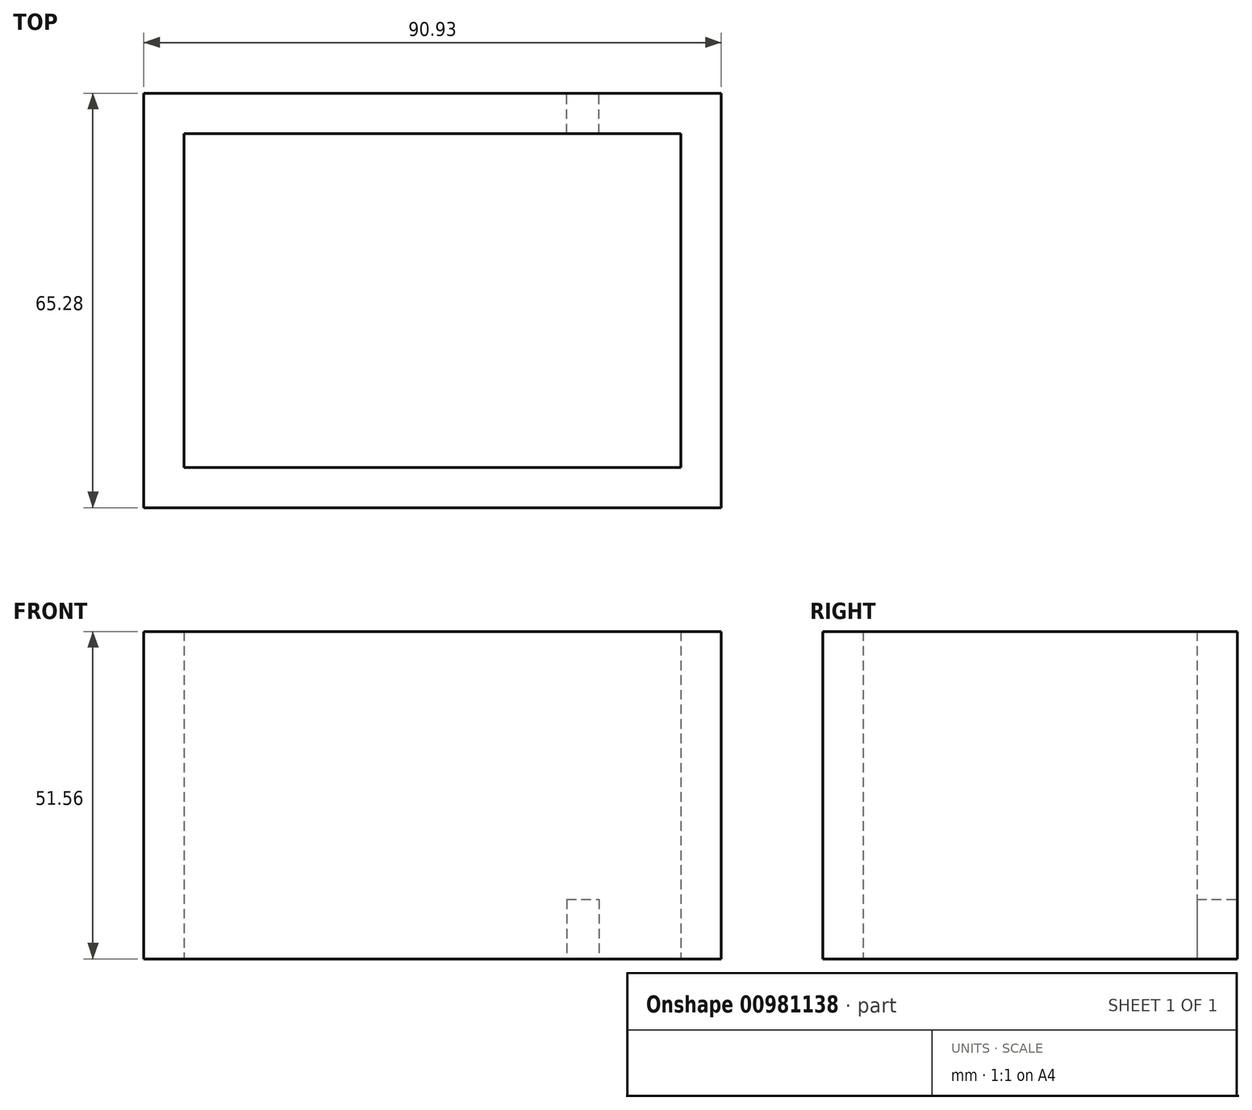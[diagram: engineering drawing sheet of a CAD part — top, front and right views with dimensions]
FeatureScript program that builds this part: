
annotation { "Feature Type Name" : "Feature", "Feature Type Description" : "" }
export const myFeature = defineFeature(function(context is Context, id is Id, definition is map)
    precondition{}
    {
        {
            var Q0;
            Q0=qCreatedBy(makeId("Top.planeOp"),FACE);
            var sketch = newSketch(context, id + "F0", { "sketchPlane" : qUnion([Q0])});
            skLineSegment(sketch, "E0.bottom", {"start": v(-31.62, 13.59) * mm, "end": v(46.6, 13.59) * mm});
            skLineSegment(sketch, "E0.top", {"start": v(-31.62, -38.99) * mm, "end": v(46.6, -38.99) * mm});
            skLineSegment(sketch, "E0.left", {"start": v(-31.62, 13.59) * mm, "end": v(-31.62, -38.99) * mm});
            skLineSegment(sketch, "E0.right", {"start": v(46.6, 13.59) * mm, "end": v(46.6, -38.99) * mm});
            skLineSegment(sketch, "E1.bottom", {"start": v(42.8, -34.16) * mm, "end": v(-28.07, -34.16) * mm});
            skLineSegment(sketch, "E1.top", {"start": v(42.8, 9.27) * mm, "end": v(-28.07, 9.27) * mm});
            skLineSegment(sketch, "E1.left", {"start": v(42.8, -34.16) * mm, "end": v(42.8, 9.27) * mm});
            skLineSegment(sketch, "E1.right", {"start": v(-28.07, -34.16) * mm, "end": v(-28.07, 9.27) * mm});
            skLineSegment(sketch, "E2.0", {"start": v(-37.97, 19.94) * mm, "end": v(-37.97, -45.34) * mm});
            skLineSegment(sketch, "E2.1", {"start": v(-37.97, 19.94) * mm, "end": v(52.96, 19.94) * mm});
            skLineSegment(sketch, "E2.2", {"start": v(52.96, 19.94) * mm, "end": v(52.96, -45.34) * mm});
            skLineSegment(sketch, "E2.3", {"start": v(-37.97, -45.34) * mm, "end": v(52.96, -45.34) * mm});
            skSolve(sketch);
        }
        {
            var Q0;
            Q0=makeQuery(id+"F0.imprint","IMPRINT",FACE,{"disambiguationData":[TD([[makeQuery(id+"F0.imprint","IMPRINT",EDGE,{"derivedFrom":sQuery(id+"F0.wireOp",EDGE,"E0.bottom")}),1.0]])]});
            extrude(context, id + "F1", {"entities" : qUnion([Q0]), "depth" : 51.56 * mm, "offsetDistance" : 25.4 * mm});
        }
        {
            var Q0;
            Q0=makeQuery(id+"F1.opExtrude","SWEPT_FACE",FACE,{"disambiguationData":[OSD([sQuery(id+"F0.wireOp",EDGE,"E2.1")])]});
            var sketch = newSketch(context, id + "F2", { "sketchPlane" : qUnion([Q0])});
            skLineSegment(sketch, "E3.bottom", {"start": v(-28.64, 9.34) * mm, "end": v(-33.68, 9.34) * mm});
            skLineSegment(sketch, "E3.top", {"start": v(-28.64, 0) * mm, "end": v(-33.68, 0) * mm});
            skLineSegment(sketch, "E3.left", {"start": v(-28.64, 9.34) * mm, "end": v(-28.64, 0) * mm});
            skLineSegment(sketch, "E3.right", {"start": v(-33.68, 9.34) * mm, "end": v(-33.68, 0) * mm});
            skSolve(sketch);
        }
        {
            var Q0;
            Q0=makeQuery(id+"F2.imprint","IMPRINT",FACE,{"disambiguationData":[TD([[makeQuery(id+"F2.imprint","IMPRINT",EDGE,{"derivedFrom":sQuery(id+"F2.wireOp",EDGE,"E3.bottom")}),1.0]])]});
            extrude(context, id + "F3", {"entities" : qUnion([Q0]), "operationType" : NewBodyOperationType.REMOVE, "oppositeDirection" : true, "depth" : 8.66 * mm, "offsetDistance" : 25.4 * mm});
        }
    });
